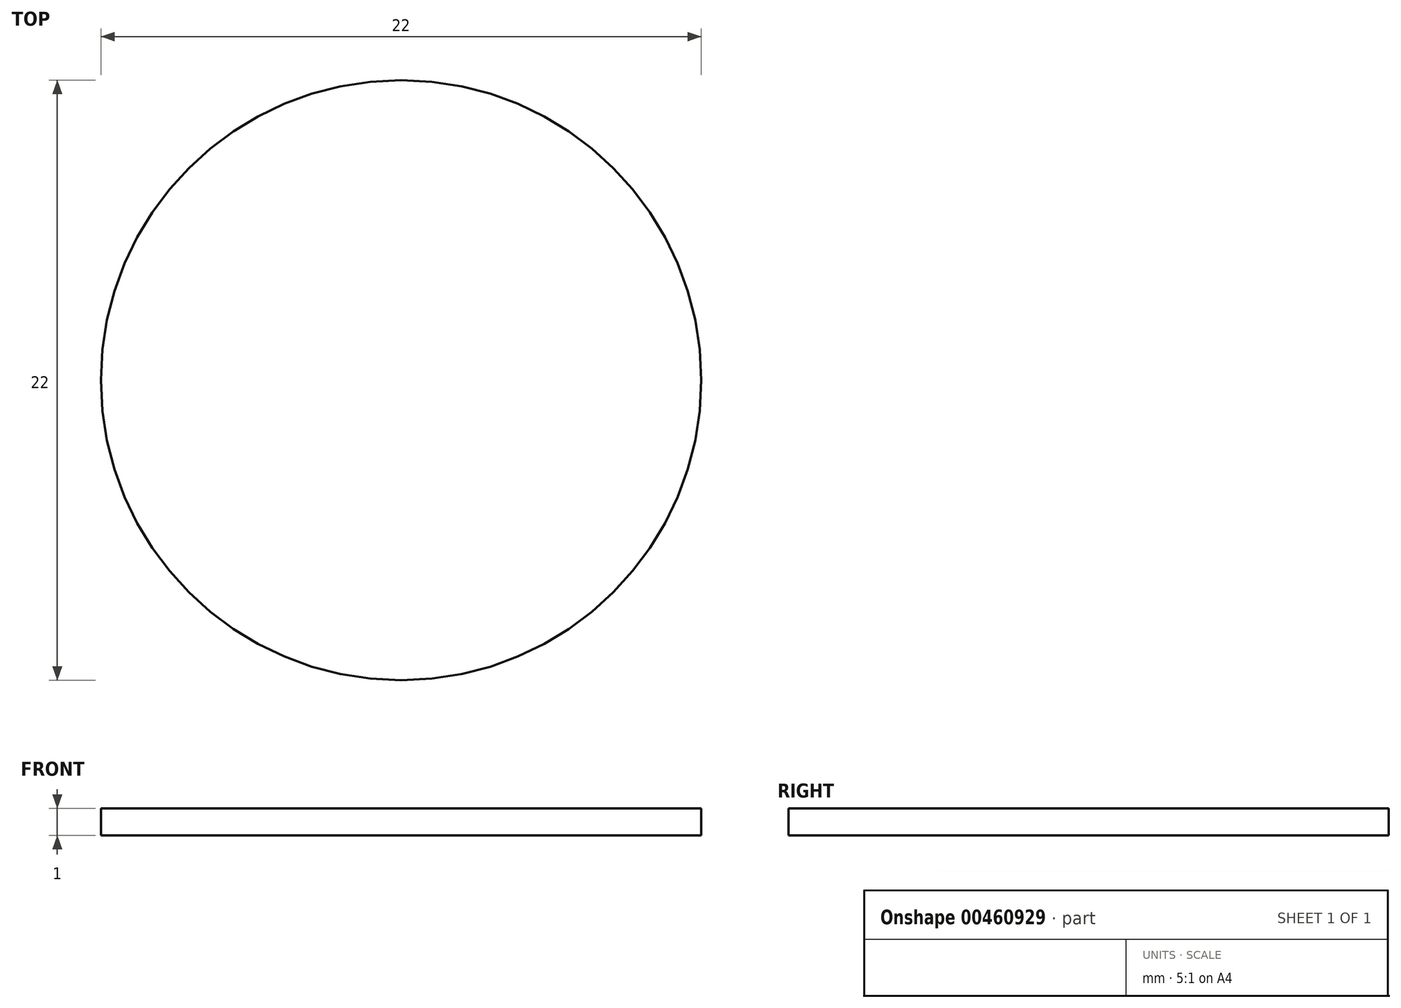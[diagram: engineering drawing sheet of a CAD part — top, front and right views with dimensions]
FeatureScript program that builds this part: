
annotation { "Feature Type Name" : "Feature", "Feature Type Description" : "" }
export const myFeature = defineFeature(function(context is Context, id is Id, definition is map)
    precondition{}
    {
        {
            var Q0;
            Q0=qCreatedBy(makeId("Top.planeOp"),FACE);
            var sketch = newSketch(context, id + "F0", { "sketchPlane" : qUnion([Q0])});
            skCircle(sketch, "E0", {"center": v(0, 0) * mm, "radius": 11 * mm});
            skSolve(sketch);
        }
        {
            var Q0;
            Q0=makeQuery(id+"F0.imprint","IMPRINT",FACE,{"disambiguationData":[TD([[makeQuery(id+"F0.imprint","IMPRINT",EDGE,{"derivedFrom":sQuery(id+"F0.wireOp",EDGE,"E0")}),1.0]])]});
            extrude(context, id + "F1", {"entities" : qUnion([Q0]), "depth" : 1 * mm, "offsetDistance" : 25 * mm});
        }
    });
